# Revit family: FU_Chair_Sandler_Flor 2-1
name_source: partatom
category: Furniture
units: mm (PartAtom-declared; Revit-internal decimal feet)

## family parameters
Always vertical = Yes
Cut with Voids When Loaded = No
OmniClass Number = 23.40.20.00
OmniClass Title = General Furniture and Specialties
Room Calculation Point = No
Shared = No
Work Plane-Based = No

## types (1)
- FU_Chair_Sandler_Flor 2-1
    Default Elevation = 0 mm  [stored 0 ft]
    Depth = 590 mm  [stored 1.9357 ft]
    Description = Chair with fully upholstered seat on a wooden frame
    Frame = Wood - Beech - Natural - V
    Height = 810 mm
    Manufacturer = Sandler
    Model = Flor 2.1
    Seat Height = 495 mm  [stored 1.62402 ft]
    URL = https://www.sandlerseating.com
    Upholstery = Fabric - Aspect - Meteora
    Width = 605 mm  [stored 1.98491 ft]

note: [stored X ft] marks values corroborated as IEEE doubles in the binary element streams (Revit-internal decimal feet)

## geometry (parser evidence)
native form markers: Sweep x4
no freeform markers — native parametric forms only
